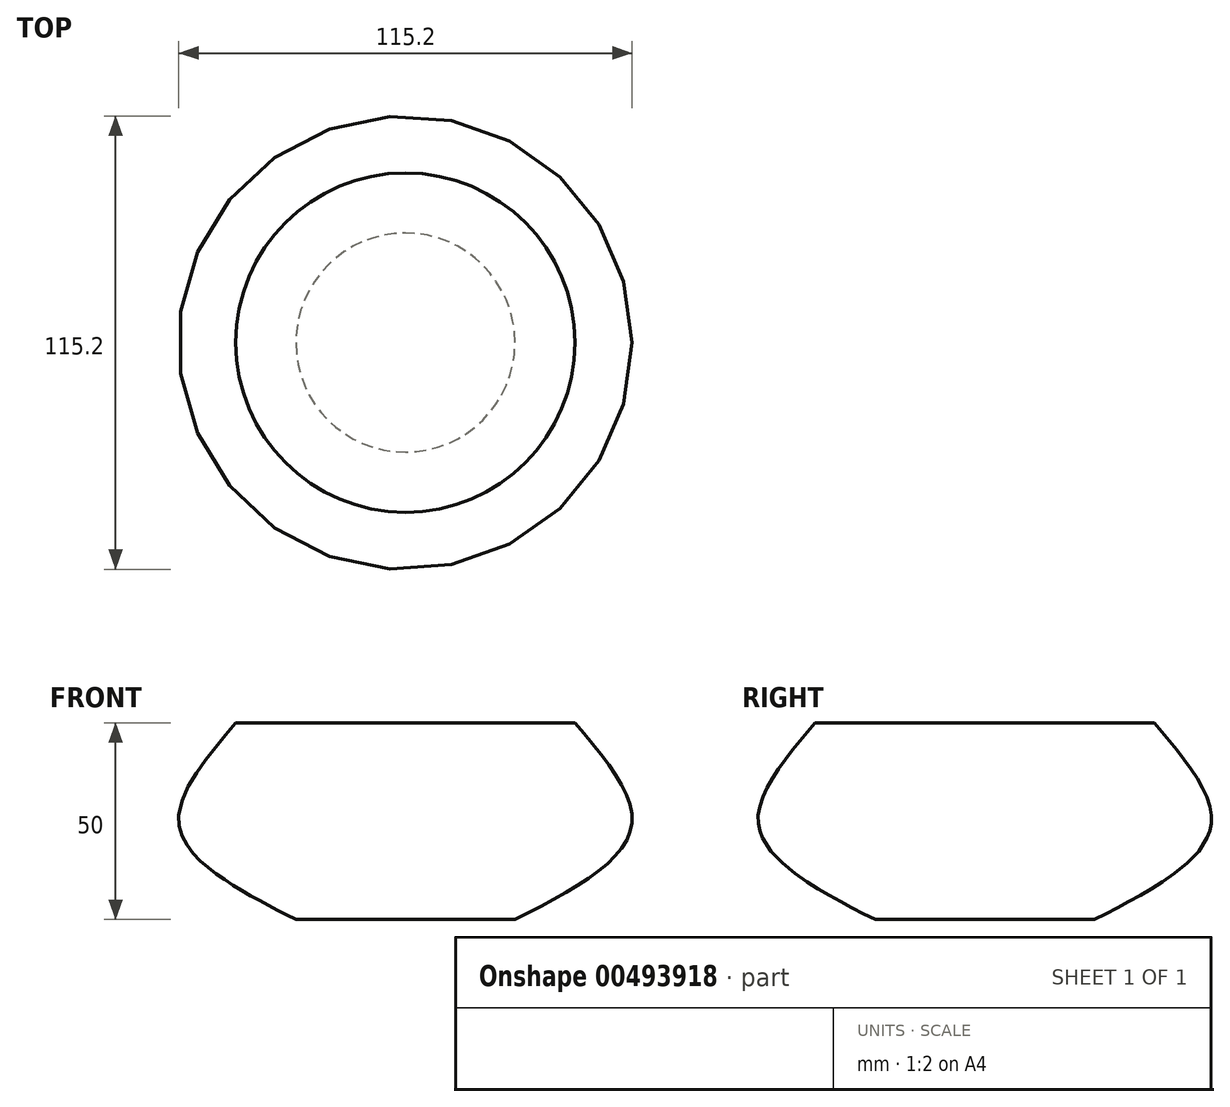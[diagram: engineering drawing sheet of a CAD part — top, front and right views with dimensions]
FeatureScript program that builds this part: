
annotation { "Feature Type Name" : "Feature", "Feature Type Description" : "" }
export const myFeature = defineFeature(function(context is Context, id is Id, definition is map)
    precondition{}
    {
        {
            var Q0;
            Q0=qCreatedBy(makeId("Top.planeOp"),FACE);
            cPlane(context, id + "F0", {"entities" : qUnion([Q0]), "cplaneType" : CPlaneType.OFFSET, "offset" : 25 * mm, "width" : 150 * mm, "height" : 150 * mm});
        }
        {
            var Q0;
            Q0=qCreatedBy(id+"F0.planeOp",FACE);
            cPlane(context, id + "F1", {"entities" : qUnion([Q0]), "cplaneType" : CPlaneType.OFFSET, "offset" : 25 * mm, "width" : 150 * mm, "height" : 150 * mm});
        }
        {
            var Q0;
            Q0=qCreatedBy(makeId("Top.planeOp"),FACE);
            var sketch = newSketch(context, id + "F2", { "sketchPlane" : qUnion([Q0])});
            skCircle(sketch, "E0", {"center": v(0, 0) * mm, "radius": 27.83 * mm});
            skSolve(sketch);
        }
        {
            var Q0;
            Q0=qCreatedBy(id+"F0.planeOp",FACE);
            var sketch = newSketch(context, id + "F3", { "sketchPlane" : qUnion([Q0])});
            skCircle(sketch, "E1", {"center": v(0, 0) * mm, "radius": 57.6 * mm});
            skSolve(sketch);
        }
        {
            var Q0;
            Q0=qCreatedBy(id+"F1.planeOp",FACE);
            var sketch = newSketch(context, id + "F4", { "sketchPlane" : qUnion([Q0])});
            skCircle(sketch, "E2", {"center": v(0, 0) * mm, "radius": 43.1 * mm});
            skSolve(sketch);
        }
        {
            var Q0;
            Q0=makeQuery(id+"F2.imprint","IMPRINT",FACE,{"disambiguationData":[TD([[makeQuery(id+"F2.imprint","IMPRINT",EDGE,{"derivedFrom":sQuery(id+"F2.wireOp",EDGE,"E0")}),1.0]])]});
            var Q1;
            Q1=makeQuery(id+"F3.imprint","IMPRINT",FACE,{"disambiguationData":[TD([[makeQuery(id+"F3.imprint","IMPRINT",EDGE,{"derivedFrom":sQuery(id+"F3.wireOp",EDGE,"E1")}),1.0]])]});
            var Q2;
            Q2=makeQuery(id+"F4.imprint","IMPRINT",FACE,{"disambiguationData":[TD([[makeQuery(id+"F4.imprint","IMPRINT",EDGE,{"derivedFrom":sQuery(id+"F4.wireOp",EDGE,"E2")}),1.0]])]});
            loft(context, id + "F5", {"sheetProfilesArray" : [{ "sheetProfileEntities" : qUnion([Q0]) }, { "sheetProfileEntities" : qUnion([Q1]) }, { "sheetProfileEntities" : qUnion([Q2]) }]});
        }
    });
